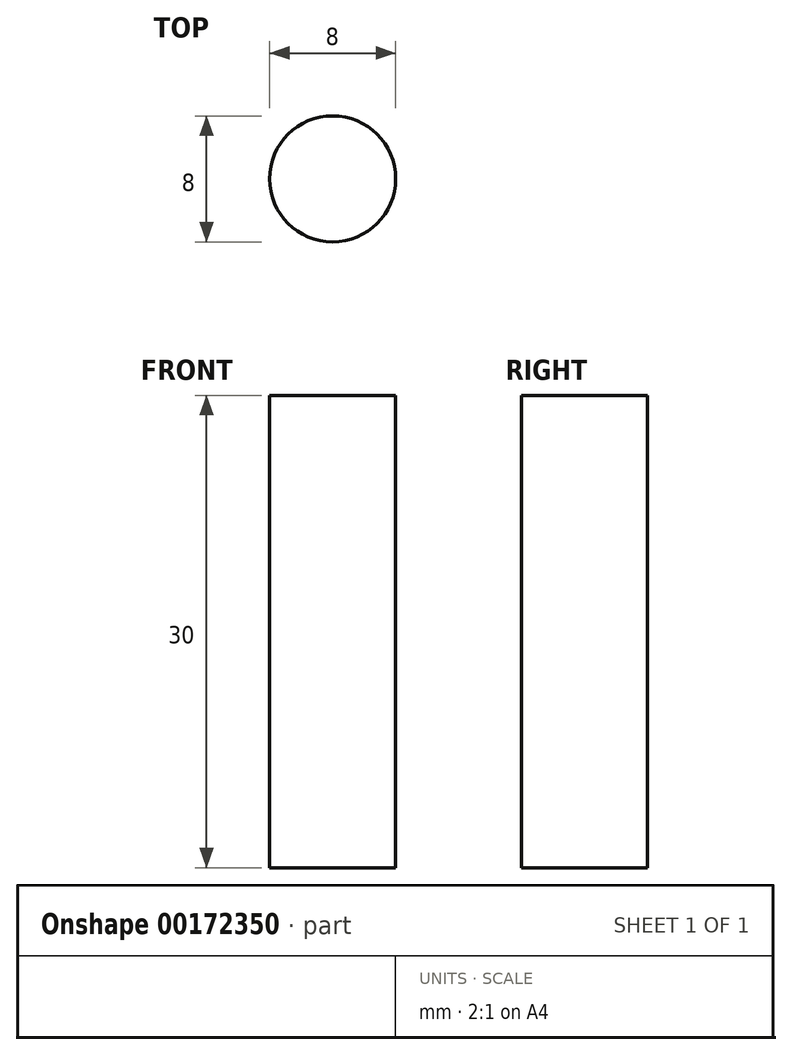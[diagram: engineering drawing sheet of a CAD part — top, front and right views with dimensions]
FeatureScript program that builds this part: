
annotation { "Feature Type Name" : "Feature", "Feature Type Description" : "" }
export const myFeature = defineFeature(function(context is Context, id is Id, definition is map)
    precondition{}
    {
        {
            var Q0;
            Q0=qCreatedBy(makeId("Top.planeOp"),FACE);
            var sketch = newSketch(context, id + "F0", { "sketchPlane" : qUnion([Q0])});
            skCircle(sketch, "E0", {"center": v(0, 0) * mm, "radius": 4 * mm});
            skSolve(sketch);
        }
        {
            var Q0;
            Q0=makeQuery(id+"F0.imprint","IMPRINT",FACE,{"disambiguationData":[TD([[makeQuery(id+"F0.imprint","IMPRINT",EDGE,{"derivedFrom":sQuery(id+"F0.wireOp",EDGE,"E0")}),1.0]])]});
            extrude(context, id + "F1", {"entities" : qUnion([Q0]), "depth" : 30 * mm});
        }
    });
